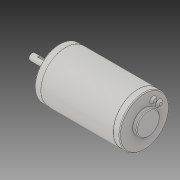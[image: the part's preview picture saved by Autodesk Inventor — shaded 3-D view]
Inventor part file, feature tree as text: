
AUTODESK INVENTOR PART (.ipt)
format: ipt  version: 2019 (Build 230136000, 136)  size: 142,336 bytes
history: native  units: in
note: dims shown in document units (in); Inventor stores cm internally (conversion verified against a paired STEP export)
features: chamfer x1
ambient origin geometry x8: Origin, YZ Plane, XZ Plane, XY Plane, X Axis, Y Axis, Z Axis, Center Point
bodies: Solid1 (feature_tree)
feature tree (1):
  chamfer  "Chamfer3"  [1 undecoded]
note: 1 required parameter value undecoded (feature->parameter linkage not recoverable at this tier; creation-order binding heuristic only, values carry confidence <= 0.55)
